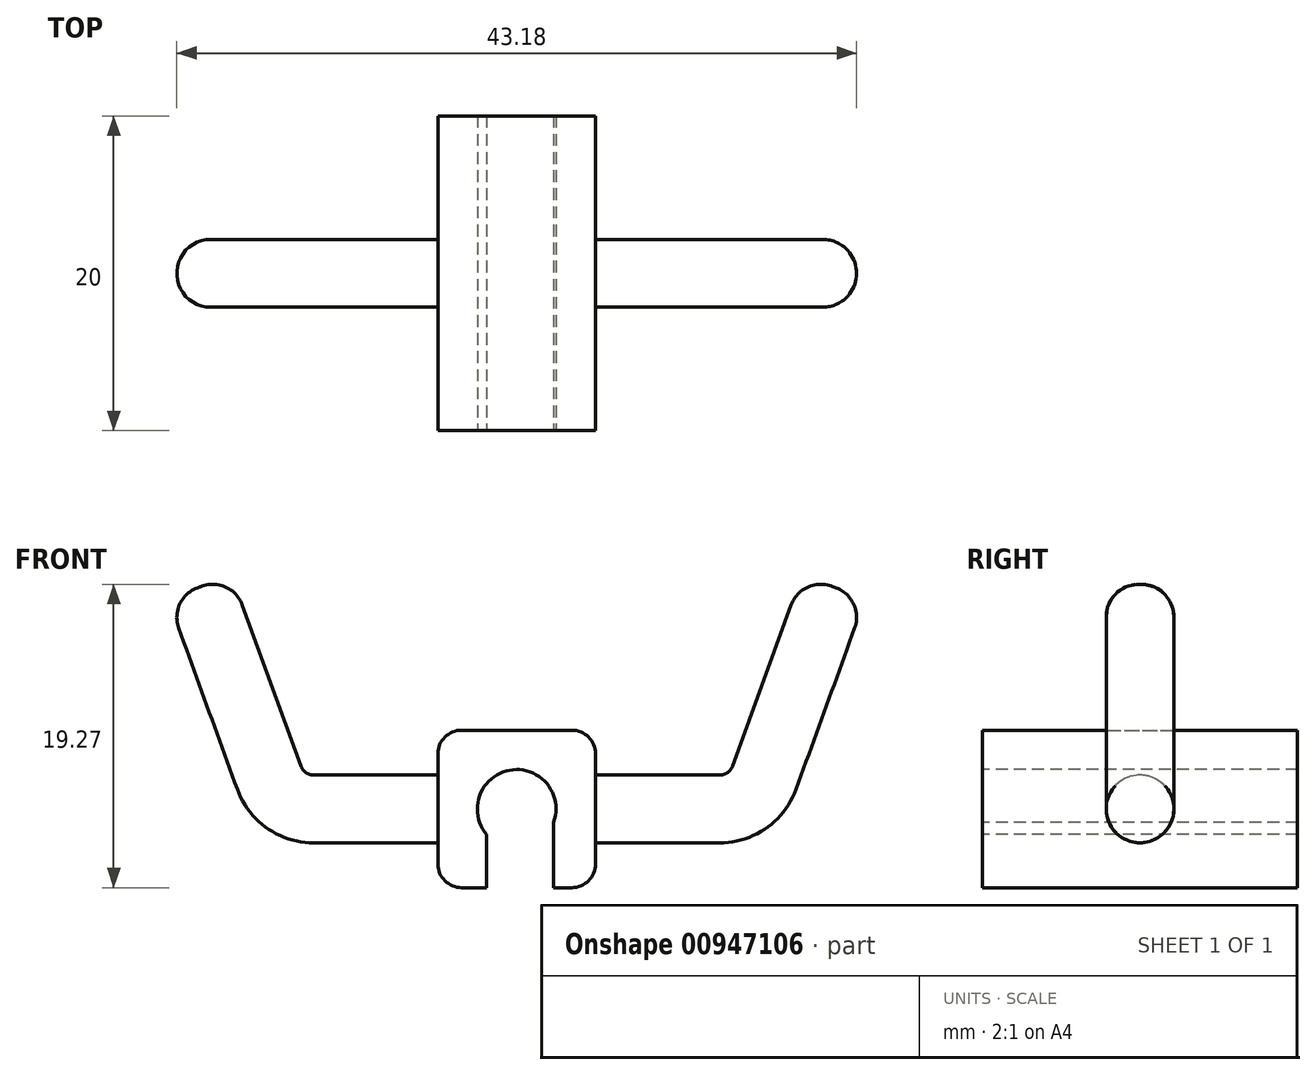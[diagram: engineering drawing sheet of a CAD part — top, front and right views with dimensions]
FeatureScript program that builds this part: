
annotation { "Feature Type Name" : "Feature", "Feature Type Description" : "" }
export const myFeature = defineFeature(function(context is Context, id is Id, definition is map)
    precondition{}
    {
        {
            var Q0;
            Q0=qCreatedBy(makeId("Front.planeOp"),FACE);
            var sketch = newSketch(context, id + "F0", { "sketchPlane" : qUnion([Q0])});
            skLineSegment(sketch, "E0.bottom", {"start": v(-5, 5) * mm, "end": v(5, 5) * mm});
            skLineSegment(sketch, "E0.top", {"start": v(-5, -5) * mm, "end": v(5, -5) * mm});
            skLineSegment(sketch, "E0.left", {"start": v(-5, 5) * mm, "end": v(-5, -5) * mm});
            skLineSegment(sketch, "E0.right", {"start": v(5, 5) * mm, "end": v(5, -5) * mm});
            skPoint(sketch, "E0.middle", {"position": v(0, 0) * mm});
            skSolve(sketch);
        }
        {
            var Q0;
            Q0=makeQuery(id+"F0.imprint","IMPRINT",FACE,{"disambiguationData":[TD([[makeQuery(id+"F0.imprint","IMPRINT",EDGE,{"derivedFrom":sQuery(id+"F0.wireOp",EDGE,"E0.bottom")}),-1.0]])]});
            extrude(context, id + "F1", {"entities" : qUnion([Q0]), "endBound" : BoundingType.SYMMETRIC, "depth" : 20 * mm, "offsetDistance" : 25 * mm});
        }
        {
            var Q0;
            Q0=qCreatedBy(makeId("Front.planeOp"),FACE);
            var sketch = newSketch(context, id + "F2", { "sketchPlane" : qUnion([Q0])});
            skLineSegment(sketch, "E1", {"start": v(0, 0) * mm, "end": v(12.9, 0) * mm});
            skLineSegment(sketch, "E2", {"start": v(15.72, 1.97) * mm, "end": v(20.13, 14.1) * mm});
            skPoint(sketch, "E3.visualSharp", {"position": v(15, 0) * mm});
            skArc(sketch, "E3.filletArc", {"start": v(12.9, 0) * mm, "mid": v(14.62, 0.54) * mm, "end": v(15.72, 1.97) * mm});
            skSolve(sketch);
        }
        {
            var Q0;
            Q0=makeQuery(id+"F1.opExtrude","CAP_FACE",FACE,{"disambiguationData":[OSD([sQuery(id+"F0.wireOp",EDGE,"E0.bottom"),sQuery(id+"F0.wireOp",EDGE,"E0.top"),sQuery(id+"F0.wireOp",EDGE,"E0.left"),sQuery(id+"F0.wireOp",EDGE,"E0.right")])],"isStart":false});
            var sketch = newSketch(context, id + "F3", { "sketchPlane" : qUnion([Q0])});
            skCircle(sketch, "E4", {"center": v(0, 0) * mm, "radius": 2.5 * mm});
            skSolve(sketch);
        }
        {
            var Q0;
            Q0=makeQuery(id+"F1.opExtrude","SWEPT_FACE",FACE,{"disambiguationData":[OSD([sQuery(id+"F0.wireOp",EDGE,"E0.right")])]});
            var sketch = newSketch(context, id + "F4", { "sketchPlane" : qUnion([Q0])});
            skCircle(sketch, "E5", {"center": v(0, 0) * mm, "radius": 2.15 * mm});
            skSolve(sketch);
        }
        {
            var Q0;
            Q0=makeQuery(id+"F4.imprint","IMPRINT",FACE,{"disambiguationData":[TD([[makeQuery(id+"F4.imprint","IMPRINT",EDGE,{"derivedFrom":sQuery(id+"F4.wireOp",EDGE,"E5")}),1.0]])]});
            var Q1;
            Q1=sQuery(id+"F2.wireOp",EDGE,"E1");
            var Q2;
            Q2=sQuery(id+"F2.wireOp",EDGE,"E3.filletArc");
            var Q3;
            Q3=sQuery(id+"F2.wireOp",EDGE,"E2");
            sweep(context, id + "F5", {"operationType" : NewBodyOperationType.ADD, "profiles" : qUnion([Q0]), "path" : qUnion([Q1, Q2, Q3])});
        }
        {
            var Q0;
            Q0=makeQuery(id+"F1.opExtrude","SWEPT_BODY",BODY,{"disambiguationData":[OSD([sQuery(id+"F0.wireOp",EDGE,"E0.bottom"),sQuery(id+"F0.wireOp",EDGE,"E0.top"),sQuery(id+"F0.wireOp",EDGE,"E0.left"),sQuery(id+"F0.wireOp",EDGE,"E0.right")])]});
            var Q1;
            Q1=qCreatedBy(makeId("Right.planeOp"),FACE);
            mirror(context, id + "F6", {"operationType" : NewBodyOperationType.ADD, "entities" : qUnion([Q0]), "mirrorPlane" : qUnion([Q1])});
        }
        {
            var Q0;
            Q0=makeQuery(id+"F3.imprint","IMPRINT",FACE,{"disambiguationData":[TD([[makeQuery(id+"F3.imprint","IMPRINT",EDGE,{"derivedFrom":sQuery(id+"F3.wireOp",EDGE,"E4")}),1.0]])]});
            extrude(context, id + "F7", {"entities" : qUnion([Q0]), "operationType" : NewBodyOperationType.REMOVE, "oppositeDirection" : true, "depth" : 25 * mm, "offsetDistance" : 25 * mm});
        }
        {
            var Q0;
            Q0=makeQuery(id+"F1.opExtrude","CAP_FACE",FACE,{"disambiguationData":[OSD([sQuery(id+"F0.wireOp",EDGE,"E0.bottom"),sQuery(id+"F0.wireOp",EDGE,"E0.top"),sQuery(id+"F0.wireOp",EDGE,"E0.left"),sQuery(id+"F0.wireOp",EDGE,"E0.right")])],"isStart":false});
            var sketch = newSketch(context, id + "F8", { "sketchPlane" : qUnion([Q0])});
            skLineSegment(sketch, "E6.bottom", {"start": v(-1.9, -6.9) * mm, "end": v(2.35, -6.9) * mm});
            skLineSegment(sketch, "E6.left", {"start": v(-1.9, -6.9) * mm, "end": v(-1.9, 0) * mm});
            skLineSegment(sketch, "E6.right", {"start": v(2.35, -6.9) * mm, "end": v(2.35, 0) * mm});
            skPoint(sketch, "E6.middle", {"position": v(0, 0) * mm});
            skLineSegment(sketch, "E7", {"start": v(2.35, 0) * mm, "end": v(-1.9, 0) * mm});
            skSolve(sketch);
        }
        {
            var Q0;
            {var subQ0=sQuery(id+"F8.wireOp",EDGE,"E6.bottom");Q0=makeQuery(id+"F8.imprint","IMPRINT",FACE,{"disambiguationData":[TD([[makeQuery(id+"F8.imprint","IMPRINT",EDGE,{"derivedFrom":subQ0}),1.0]])]});}
            var Q1;
            {var subQ0=sQuery(id+"F8.wireOp",EDGE,"E6.left");var subQ1=makeQuery(id+"F1.opExtrude","CAP_EDGE",EDGE,{"disambiguationData":[OSD([sQuery(id+"F0.wireOp",EDGE,"E0.top")])],"isStart":false});var subQ2=makeQuery(id+"F8.imprint","INTERSECT",VERTEX,{"derivedFrom":[subQ1,subQ0]});Q1=makeQuery(id+"F8.imprint","IMPRINT",FACE,{"disambiguationData":[TD([[makeQuery(id+"F8.imprint","IMPRINT",EDGE,{"disambiguationData":[TD([[subQ2,-1.0]])],"derivedFrom":subQ0}),-1.0]])]});}
            var Q2;
            {var subQ0=sQuery(id+"F8.wireOp",EDGE,"E7");Q2=makeQuery(id+"F8.imprint","IMPRINT",FACE,{"disambiguationData":[TD([[makeQuery(id+"F8.imprint","IMPRINT",EDGE,{"derivedFrom":subQ0}),1.0]])]});}
            extrude(context, id + "F9", {"entities" : qUnion([Q0, Q1, Q2]), "operationType" : NewBodyOperationType.REMOVE, "endBound" : BoundingType.UP_TO_NEXT, "oppositeDirection" : true, "depth" : 25 * mm, "offsetDistance" : 25 * mm});
        }
        {
            var Q0;
            Q0=makeQuery(id+"F1.opExtrude","SWEPT_EDGE",EDGE,{"disambiguationData":[OSD([sQuery(id+"F0.wireOp",EDGE,"E0.bottom"),sQuery(id+"F0.wireOp",EDGE,"E0.right")])]});
            var Q1;
            Q1=makeQuery(id+"F1.opExtrude","SWEPT_EDGE",EDGE,{"disambiguationData":[OSD([sQuery(id+"F0.wireOp",EDGE,"E0.bottom"),sQuery(id+"F0.wireOp",EDGE,"E0.left")])]});
            var Q2;
            Q2=makeQuery(id+"F1.opExtrude","SWEPT_EDGE",EDGE,{"disambiguationData":[OSD([sQuery(id+"F0.wireOp",EDGE,"E0.top"),sQuery(id+"F0.wireOp",EDGE,"E0.right")])]});
            var Q3;
            Q3=makeQuery(id+"F1.opExtrude","SWEPT_EDGE",EDGE,{"disambiguationData":[OSD([sQuery(id+"F0.wireOp",EDGE,"E0.top"),sQuery(id+"F0.wireOp",EDGE,"E0.left")])]});
            fillet(context, id + "F10", {"entities" : qUnion([Q0, Q1, Q2, Q3]), "radius" : 1.5 * mm, "tangentPropagation" : true, "allowEdgeOverflow" : false});
        }
        {
            var Q0;
            Q0=makeQuery(id+"F6.opPattern","COPY",EDGE,{"derivedFrom":makeQuery(id+"F5.opSweep","CAP_EDGE",EDGE,{"disambiguationData":[OSD([sQuery(id+"F2.wireOp",VERTEX,"E2.end"),sQuery(id+"F4.wireOp",EDGE,"E5")])],"isStart":false}),"instanceName":"1"});
            var Q1;
            Q1=makeQuery(id+"F5.opSweep","CAP_EDGE",EDGE,{"disambiguationData":[OSD([sQuery(id+"F2.wireOp",VERTEX,"E2.end"),sQuery(id+"F4.wireOp",EDGE,"E5")])],"isStart":false});
            fillet(context, id + "F11", {"entities" : qUnion([Q0, Q1]), "radius" : 2 * mm, "tangentPropagation" : true, "allowEdgeOverflow" : false});
        }
    });
